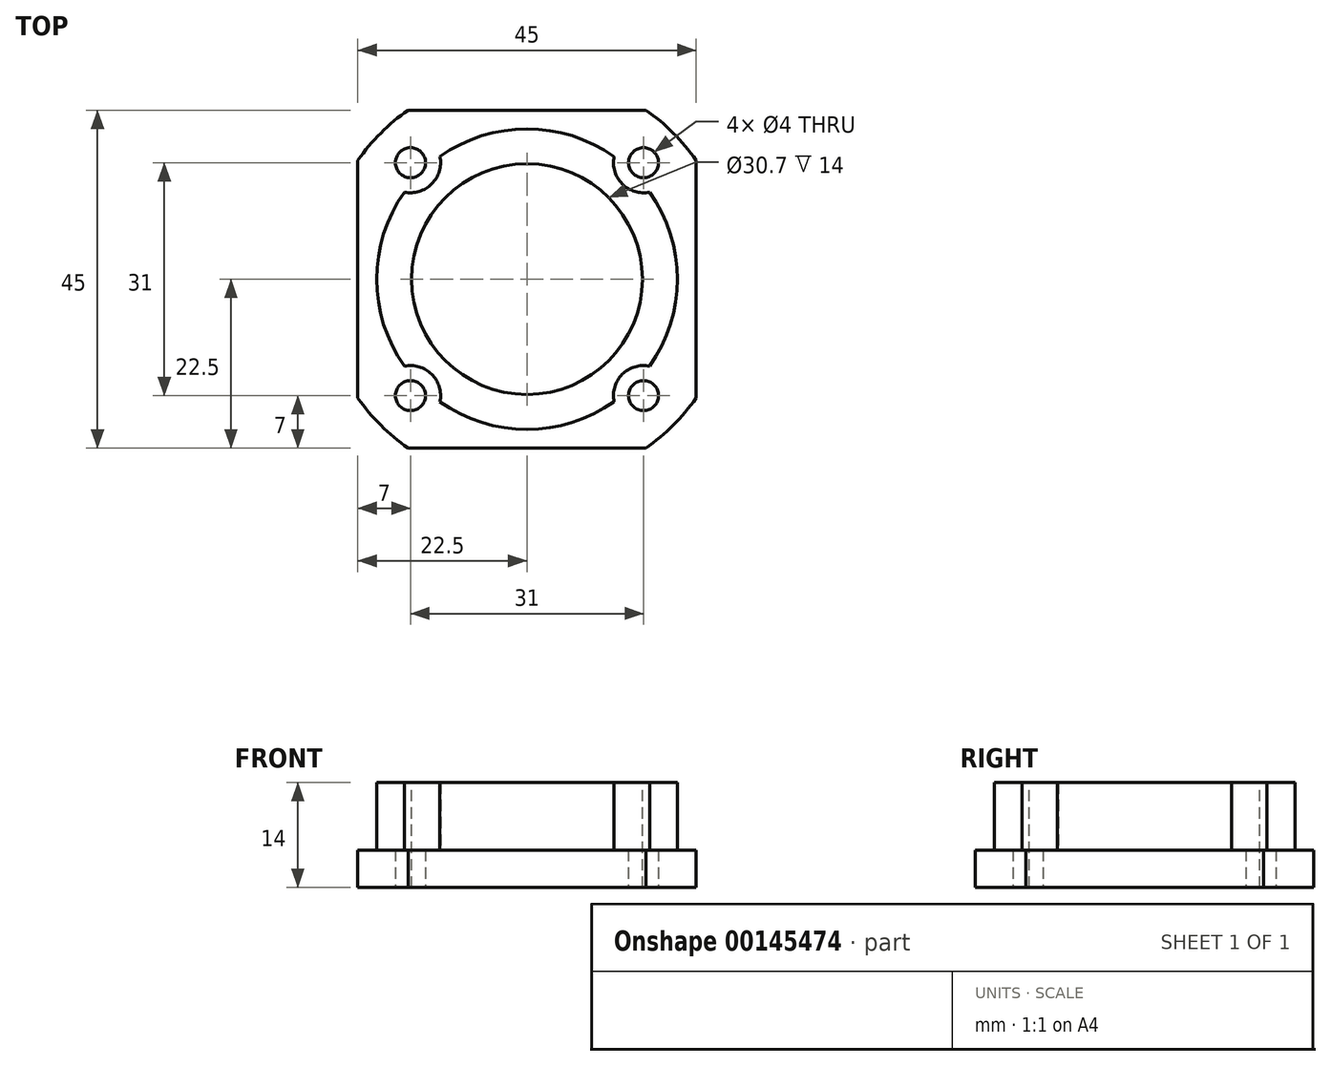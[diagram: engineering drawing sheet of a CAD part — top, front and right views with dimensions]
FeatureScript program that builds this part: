
annotation { "Feature Type Name" : "Feature", "Feature Type Description" : "" }
export const myFeature = defineFeature(function(context is Context, id is Id, definition is map)
    precondition{}
    {
        {
            var Q0;
            Q0=qCreatedBy(makeId("Top.planeOp"),FACE);
            var sketch = newSketch(context, id + "F0", { "sketchPlane" : qUnion([Q0])});
            skLineSegment(sketch, "E0.bottom", {"start": v(22.5, -22.5) * mm, "end": v(-22.5, -22.5) * mm});
            skLineSegment(sketch, "E0.top", {"start": v(22.5, 22.5) * mm, "end": v(-22.5, 22.5) * mm});
            skLineSegment(sketch, "E0.left", {"start": v(22.5, -22.5) * mm, "end": v(22.5, 22.5) * mm});
            skLineSegment(sketch, "E0.right", {"start": v(-22.5, -22.5) * mm, "end": v(-22.5, 22.5) * mm});
            skPoint(sketch, "E0.middle", {"position": v(0, 0) * mm});
            skSolve(sketch);
        }
        {
            var Q0;
            Q0 = qSketchRegion(id + "F0", true);
            extrude(context, id + "F1", {"entities" : qUnion([Q0]), "depth" : 5 * mm});
        }
        {
            var Q0;
            Q0=makeQuery(id+"F1.opExtrude","CAP_FACE",FACE,{"disambiguationData":[OSD([sQuery(id+"F0.wireOp",EDGE,"KqD3YALu-Ptcp-6ljj-zWQT-Y2KtIa6KFCM0"),sQuery(id+"F0.wireOp",EDGE,"E0.bottom"),sQuery(id+"F0.wireOp",EDGE,"E0.top"),sQuery(id+"F0.wireOp",EDGE,"E0.left"),sQuery(id+"F0.wireOp",EDGE,"E0.right")])],"isStart":false});
            var sketch = newSketch(context, id + "F2", { "sketchPlane" : qUnion([Q0])});
            skLineSegment(sketch, "E1.top", {"start": v(-22.5, -22.5) * mm, "end": v(22.5, -22.5) * mm});
            skCircle(sketch, "E2", {"center": v(0, 0) * mm, "radius": 20 * mm});
            skSolve(sketch);
        }
        {
            var Q0;
            Q0 = qSketchRegion(id + "F2", true);
            extrude(context, id + "F3", {"entities" : qUnion([Q0]), "operationType" : NewBodyOperationType.ADD, "depth" : 9 * mm});
        }
        {
            var Q0;
            Q0=makeQuery(id+"F1.opExtrude","CAP_FACE",FACE,{"disambiguationData":[OSD([sQuery(id+"F0.wireOp",EDGE,"KqD3YALu-Ptcp-6ljj-zWQT-Y2KtIa6KFCM0"),sQuery(id+"F0.wireOp",EDGE,"E0.bottom"),sQuery(id+"F0.wireOp",EDGE,"E0.top"),sQuery(id+"F0.wireOp",EDGE,"E0.left"),sQuery(id+"F0.wireOp",EDGE,"E0.right")])],"isStart":true});
            var sketch = newSketch(context, id + "F4", { "sketchPlane" : qUnion([Q0])});
            skCircle(sketch, "E3", {"center": v(-15.5, 15.5) * mm, "radius": 2 * mm});
            skCircle(sketch, "E4.0.1.0", {"center": v(-15.5, -15.5) * mm, "radius": 2 * mm});
            skCircle(sketch, "E4.1.0.0", {"center": v(15.5, 15.5) * mm, "radius": 2 * mm});
            skCircle(sketch, "E4.1.1.0", {"center": v(15.5, -15.5) * mm, "radius": 2 * mm});
            skLineSegment(sketch, "E4.direction1", {"start": v(-15.5, 15.5) * mm, "end": v(15.5, 15.5) * mm, "construction": true});
            skLineSegment(sketch, "E4.direction2", {"start": v(-15.5, 15.5) * mm, "end": v(-15.5, -15.5) * mm, "construction": true});
            skSolve(sketch);
        }
        {
            var Q0;
            Q0 = qSketchRegion(id + "F4", true);
            extrude(context, id + "F5", {"entities" : qUnion([Q0]), "operationType" : NewBodyOperationType.REMOVE, "oppositeDirection" : true, "depth" : 25 * mm});
        }
        {
            var Q0;
            {var subQ0=sQuery(id+"F0.wireOp",EDGE,"E0.right");var subQ1=sQuery(id+"F0.wireOp",EDGE,"E0.left");var subQ2=sQuery(id+"F0.wireOp",EDGE,"E0.top");var subQ3=sQuery(id+"F0.wireOp",EDGE,"E0.bottom");Q0=makeQuery(id+"F3.boolean.opBoolean","SPLIT",FACE,{"disambiguationData":[TD([makeQuery(id+"F1.opExtrude","SWEPT_FACE",FACE,{"disambiguationData":[OSD([subQ3])]})])],"derivedFrom":makeQuery(id+"F1.opExtrude","CAP_FACE",FACE,{"disambiguationData":[OSD([sQuery(id+"F0.wireOp",EDGE,"KqD3YALu-Ptcp-6ljj-zWQT-Y2KtIa6KFCM0"),subQ3,subQ2,subQ1,subQ0])],"isStart":false})});}
            var sketch = newSketch(context, id + "F6", { "sketchPlane" : qUnion([Q0])});
            skCircle(sketch, "E5", {"center": v(15.5, -15.5) * mm, "radius": 4 * mm});
            skCircle(sketch, "E6", {"center": v(-15.5, -15.5) * mm, "radius": 4 * mm});
            skCircle(sketch, "E7", {"center": v(15.5, 15.5) * mm, "radius": 4 * mm});
            skCircle(sketch, "E8", {"center": v(-15.5, 15.5) * mm, "radius": 4 * mm});
            skSolve(sketch);
        }
        {
            var Q0;
            Q0 = qSketchRegion(id + "F6", true);
            extrude(context, id + "F7", {"entities" : qUnion([Q0]), "operationType" : NewBodyOperationType.REMOVE, "depth" : 25 * mm});
        }
        {
            var Q0;
            Q0=makeQuery(id+"F3.opExtrude","CAP_FACE",FACE,{"disambiguationData":[OSD([sQuery(id+"F2.wireOp",EDGE,"E2")])],"isStart":false});
            var sketch = newSketch(context, id + "F8", { "sketchPlane" : qUnion([Q0])});
            skCircle(sketch, "E9", {"center": v(0, 0) * mm, "radius": 15.35 * mm});
            skSolve(sketch);
        }
        {
            var Q0;
            Q0 = qSketchRegion(id + "F8", true);
            extrude(context, id + "F9", {"entities" : qUnion([Q0]), "operationType" : NewBodyOperationType.REMOVE, "oppositeDirection" : true, "depth" : 25 * mm});
        }
        {
            var Q0;
            Q0=makeQuery(id+"F1.opExtrude","CAP_FACE",FACE,{"disambiguationData":[OSD([sQuery(id+"F0.wireOp",EDGE,"E0.bottom"),sQuery(id+"F0.wireOp",EDGE,"E0.top"),sQuery(id+"F0.wireOp",EDGE,"E0.left"),sQuery(id+"F0.wireOp",EDGE,"E0.right")])],"isStart":true});
            var sketch = newSketch(context, id + "F10", { "sketchPlane" : qUnion([Q0])});
            skCircle(sketch, "E10", {"center": v(0, 0) * mm, "radius": 27.5 * mm});
            skCircle(sketch, "E11", {"center": v(0, 0) * mm, "radius": 45.14 * mm});
            skSolve(sketch);
        }
        {
            var Q0;
            Q0 = qSketchRegion(id + "F10", true);
            extrude(context, id + "F11", {"entities" : qUnion([Q0]), "operationType" : NewBodyOperationType.REMOVE, "oppositeDirection" : true, "depth" : 25 * mm});
        }
    });
